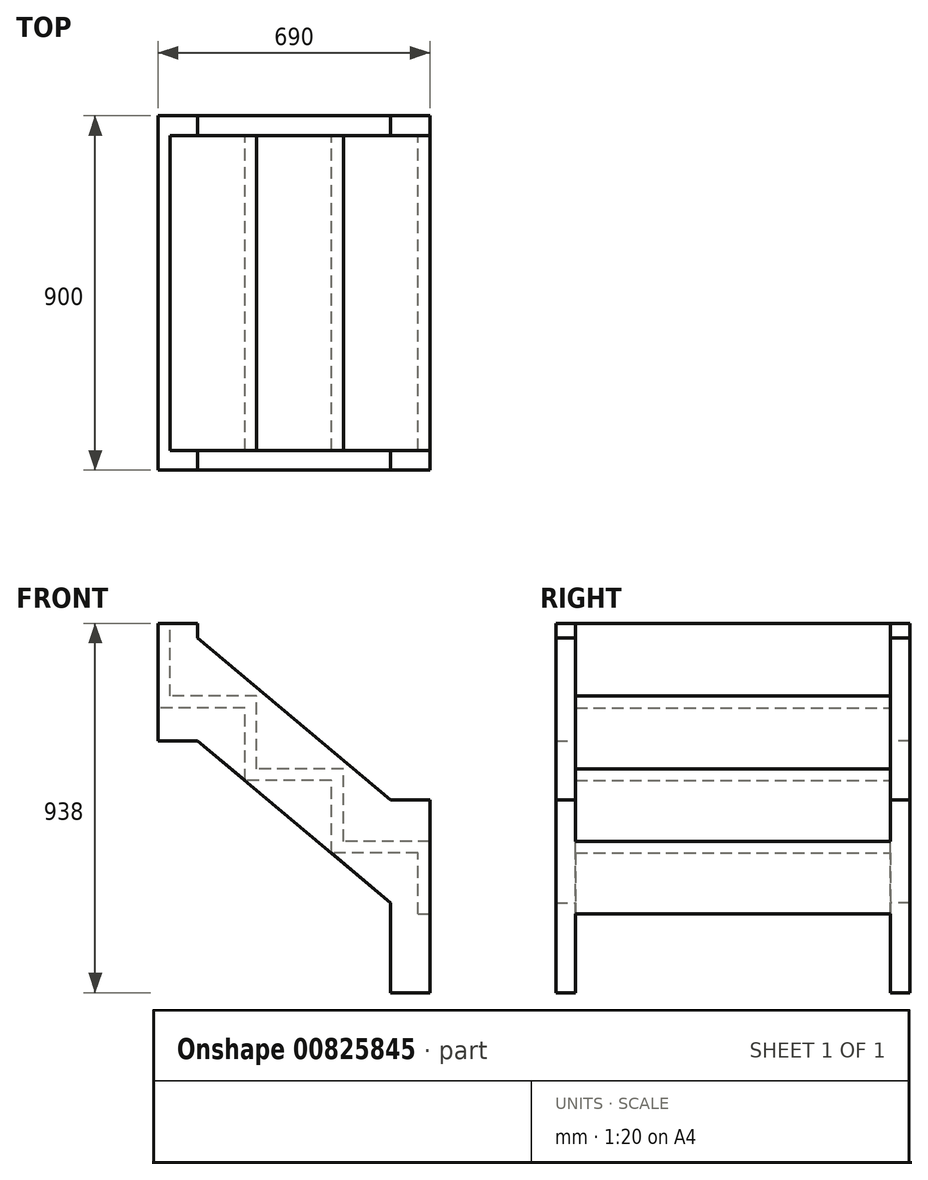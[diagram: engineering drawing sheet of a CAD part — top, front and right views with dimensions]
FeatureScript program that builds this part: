
annotation { "Feature Type Name" : "Feature", "Feature Type Description" : "" }
export const myFeature = defineFeature(function(context is Context, id is Id, definition is map)
    precondition{}
    {
        {
            var Q0;
            Q0=qCreatedBy(makeId("Front.planeOp"),FACE);
            var sketch = newSketch(context, id + "F0", { "sketchPlane" : qUnion([Q0])});
            skLineSegment(sketch, "E0", {"start": v(0, 0) * mm, "end": v(0, 184.5) * mm});
            skLineSegment(sketch, "E1.0", {"start": v(-220, 154.5) * mm, "end": v(-220, 369) * mm});
            skLineSegment(sketch, "E2.0", {"start": v(-440, 339) * mm, "end": v(-440, 553.5) * mm});
            skLineSegment(sketch, "E3.0", {"start": v(-660, 523.5) * mm, "end": v(-660, 738) * mm});
            skLineSegment(sketch, "E4.0", {"start": v(0, 184.5) * mm, "end": v(-220, 184.5) * mm});
            skLineSegment(sketch, "E5.0", {"start": v(-220, 369) * mm, "end": v(-440, 369) * mm});
            skLineSegment(sketch, "E6.trimOffspring", {"start": v(-440, 553.5) * mm, "end": v(-660, 553.5) * mm});
            skLineSegment(sketch, "E7.0", {"start": v(-660, 738) * mm, "end": v(-690, 738) * mm});
            skPoint(sketch, "E8.orphan", {"position": v(-742.16, 0) * mm});
            skLineSegment(sketch, "E9.0", {"start": v(0, 154.5) * mm, "end": v(-220, 154.5) * mm});
            skLineSegment(sketch, "E10.0", {"start": v(-220, 339) * mm, "end": v(-440, 339) * mm});
            skLineSegment(sketch, "E11.0", {"start": v(-440, 523.5) * mm, "end": v(-660, 523.5) * mm});
            skLineSegment(sketch, "E12.0", {"start": v(-30, 0) * mm, "end": v(-30, 184.5) * mm});
            skLineSegment(sketch, "E13.0", {"start": v(-250, 154.5) * mm, "end": v(-250, 369) * mm});
            skLineSegment(sketch, "E14.0", {"start": v(-470, 339) * mm, "end": v(-470, 553.5) * mm});
            skLineSegment(sketch, "E15", {"start": v(-440, 339) * mm, "end": v(-470, 339) * mm});
            skLineSegment(sketch, "E16", {"start": v(-470, 339) * mm, "end": v(-470, 369) * mm});
            skLineSegment(sketch, "E17", {"start": v(-470, 369) * mm, "end": v(-440, 369) * mm});
            skLineSegment(sketch, "E18", {"start": v(-220, 184.5) * mm, "end": v(-250, 184.5) * mm});
            skLineSegment(sketch, "E19", {"start": v(-250, 184.5) * mm, "end": v(-250, 154.5) * mm});
            skLineSegment(sketch, "E20", {"start": v(-250, 154.5) * mm, "end": v(-220, 154.5) * mm});
            skLineSegment(sketch, "E21", {"start": v(-30, 0) * mm, "end": v(0, 0) * mm});
            skLineSegment(sketch, "E22.0", {"start": v(-690, 523.5) * mm, "end": v(-690, 738) * mm});
            skLineSegment(sketch, "E23", {"start": v(-660, 553.5) * mm, "end": v(-690, 553.5) * mm});
            skLineSegment(sketch, "E24", {"start": v(-690, 553.5) * mm, "end": v(-690, 523.5) * mm});
            skLineSegment(sketch, "E25", {"start": v(-690, 523.5) * mm, "end": v(-660, 523.5) * mm});
            skPoint(sketch, "E26.orphan", {"position": v(-660, 0) * mm});
            skPoint(sketch, "E27.orphan", {"position": v(-250, 0) * mm});
            skSolve(sketch);
        }
        {
            var Q0;
            Q0 = qSketchRegion(id + "F0", true);
            extrude(context, id + "F1", {"entities" : qUnion([Q0]), "depth" : 800 * mm, "offsetDistance" : 25 * mm});
        }
        {
            var Q0;
            Q0=makeQuery(id+"F1.opExtrude","CAP_FACE",FACE,{"disambiguationData":[OSD([sQuery(id+"F0.wireOp",EDGE,"E0"),sQuery(id+"F0.wireOp",EDGE,"E1.0"),sQuery(id+"F0.wireOp",EDGE,"E2.0"),sQuery(id+"F0.wireOp",EDGE,"E3.0"),sQuery(id+"F0.wireOp",EDGE,"E4.0"),sQuery(id+"F0.wireOp",EDGE,"E5.0"),sQuery(id+"F0.wireOp",EDGE,"E6.trimOffspring"),sQuery(id+"F0.wireOp",EDGE,"E7.0"),sQuery(id+"F0.wireOp",EDGE,"E9.0"),sQuery(id+"F0.wireOp",EDGE,"E10.0"),sQuery(id+"F0.wireOp",EDGE,"E11.0"),sQuery(id+"F0.wireOp",EDGE,"E12.0"),sQuery(id+"F0.wireOp",EDGE,"E13.0"),sQuery(id+"F0.wireOp",EDGE,"E14.0"),sQuery(id+"F0.wireOp",EDGE,"E15"),sQuery(id+"F0.wireOp",EDGE,"E16"),sQuery(id+"F0.wireOp",EDGE,"E19"),sQuery(id+"F0.wireOp",EDGE,"E20"),sQuery(id+"F0.wireOp",EDGE,"E21"),sQuery(id+"F0.wireOp",EDGE,"E22.0"),sQuery(id+"F0.wireOp",EDGE,"E24"),sQuery(id+"F0.wireOp",EDGE,"E25")])],"isStart":false});
            var sketch = newSketch(context, id + "F2", { "sketchPlane" : qUnion([Q0])});
            skLineSegment(sketch, "E28", {"start": v(-690, 523.5) * mm, "end": v(-100, 28.7) * mm});
            skLineSegment(sketch, "E29", {"start": v(0, 303.5) * mm, "end": v(0, -200) * mm});
            skLineSegment(sketch, "E30", {"start": v(-690, 738) * mm, "end": v(-690, 439.64) * mm});
            skLineSegment(sketch, "E31.0", {"start": v(-590, 700.66) * mm, "end": v(-100, 289.73) * mm});
            skLineSegment(sketch, "E32.0", {"start": v(-590, 738) * mm, "end": v(-590, 439.64) * mm});
            skLineSegment(sketch, "E33.0", {"start": v(-100, 303.5) * mm, "end": v(-100, -200) * mm});
            skLineSegment(sketch, "E34", {"start": v(-100, 289.73) * mm, "end": v(0, 289.73) * mm});
            skLineSegment(sketch, "E35", {"start": v(-690, 738) * mm, "end": v(-590, 738) * mm});
            skLineSegment(sketch, "E36", {"start": v(-590, 439.64) * mm, "end": v(-690, 439.64) * mm});
            skPoint(sketch, "E37.orphan", {"position": v(-690, 868.42) * mm});
            skLineSegment(sketch, "E38", {"start": v(0, -200) * mm, "end": v(-100, -200) * mm});
            skSolve(sketch);
        }
        {
            var Q0;
            Q0 = qSketchRegion(id + "F2", true);
            extrude(context, id + "F3", {"entities" : qUnion([Q0]), "operationType" : NewBodyOperationType.ADD, "depth" : 50 * mm, "offsetDistance" : 25 * mm});
        }
        {
            var Q0;
            Q0=makeQuery(id+"F1.opExtrude","CAP_FACE",FACE,{"disambiguationData":[OSD([sQuery(id+"F0.wireOp",EDGE,"E0"),sQuery(id+"F0.wireOp",EDGE,"E1.0"),sQuery(id+"F0.wireOp",EDGE,"E2.0"),sQuery(id+"F0.wireOp",EDGE,"E3.0"),sQuery(id+"F0.wireOp",EDGE,"E4.0"),sQuery(id+"F0.wireOp",EDGE,"E5.0"),sQuery(id+"F0.wireOp",EDGE,"E6.trimOffspring"),sQuery(id+"F0.wireOp",EDGE,"E7.0"),sQuery(id+"F0.wireOp",EDGE,"E9.0"),sQuery(id+"F0.wireOp",EDGE,"E10.0"),sQuery(id+"F0.wireOp",EDGE,"E11.0"),sQuery(id+"F0.wireOp",EDGE,"E12.0"),sQuery(id+"F0.wireOp",EDGE,"E13.0"),sQuery(id+"F0.wireOp",EDGE,"E14.0"),sQuery(id+"F0.wireOp",EDGE,"E15"),sQuery(id+"F0.wireOp",EDGE,"E16"),sQuery(id+"F0.wireOp",EDGE,"E19"),sQuery(id+"F0.wireOp",EDGE,"E20"),sQuery(id+"F0.wireOp",EDGE,"E21"),sQuery(id+"F0.wireOp",EDGE,"E22.0"),sQuery(id+"F0.wireOp",EDGE,"E24"),sQuery(id+"F0.wireOp",EDGE,"E25")])],"isStart":true});
            var sketch = newSketch(context, id + "F4", { "sketchPlane" : qUnion([Q0])});
            skPoint(sketch, "E39.orphan", {"position": v(-739.38, 1115.38) * mm});
            skLineSegment(sketch, "E40.MirrorCS", {"start": v(0, -200) * mm, "end": v(100, -200) * mm});
            skLineSegment(sketch, "E41.MirrorCS", {"start": v(590, 439.64) * mm, "end": v(690, 439.64) * mm});
            skLineSegment(sketch, "E42.MirrorCS", {"start": v(100, 289.73) * mm, "end": v(0, 289.73) * mm});
            skLineSegment(sketch, "E43.MirrorCS", {"start": v(690, 738) * mm, "end": v(590, 738) * mm});
            skLineSegment(sketch, "E44.MirrorCS", {"start": v(690, 738) * mm, "end": v(690, 439.64) * mm});
            skPoint(sketch, "E45.MirrorP", {"position": v(739.38, 1115.38) * mm});
            skLineSegment(sketch, "E46.MirrorCS", {"start": v(100, 289.73) * mm, "end": v(100, -200) * mm});
            skLineSegment(sketch, "E47.MirrorCS", {"start": v(0, 289.73) * mm, "end": v(0, -200) * mm});
            skLineSegment(sketch, "E48.MirrorCS", {"start": v(590, 439.64) * mm, "end": v(100, 28.7) * mm});
            skLineSegment(sketch, "E49.MirrorCS", {"start": v(590, 700.66) * mm, "end": v(100, 289.73) * mm});
            skLineSegment(sketch, "E50.MirrorCS", {"start": v(590, 738) * mm, "end": v(590, 439.64) * mm});
            skSolve(sketch);
        }
        {
            var Q0;
            Q0 = qSketchRegion(id + "F4", true);
            extrude(context, id + "F5", {"entities" : qUnion([Q0]), "operationType" : NewBodyOperationType.ADD, "depth" : 50 * mm, "offsetDistance" : 25 * mm});
        }
    });
